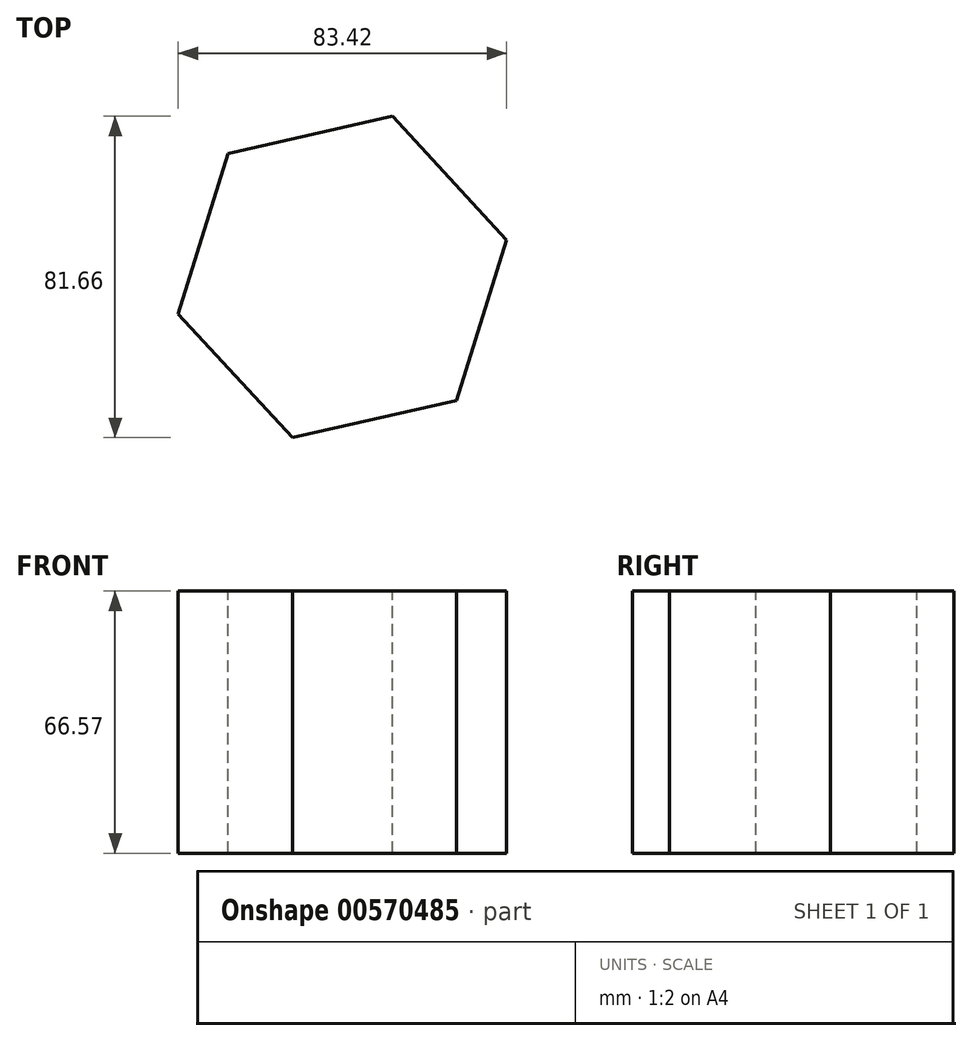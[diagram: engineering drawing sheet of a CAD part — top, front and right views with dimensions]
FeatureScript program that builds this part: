
annotation { "Feature Type Name" : "Feature", "Feature Type Description" : "" }
export const myFeature = defineFeature(function(context is Context, id is Id, definition is map)
    precondition{}
    {
        {
            var Q0;
            Q0=qCreatedBy(makeId("Top.planeOp"),FACE);
            var sketch = newSketch(context, id + "F0", { "sketchPlane" : qUnion([Q0])});
            skLineSegment(sketch, "E0.0", {"start": v(12.7, 40.83) * mm, "end": v(41.7, 9.42) * mm});
            skLineSegment(sketch, "E0.1", {"start": v(41.7, 9.42) * mm, "end": v(29.01, -31.4) * mm});
            skLineSegment(sketch, "E0.2", {"start": v(29.01, -31.4) * mm, "end": v(-12.7, -40.83) * mm});
            skLineSegment(sketch, "E0.3", {"start": v(-12.7, -40.83) * mm, "end": v(-41.7, -9.42) * mm});
            skLineSegment(sketch, "E0.4", {"start": v(-41.7, -9.42) * mm, "end": v(-29.01, 31.4) * mm});
            skLineSegment(sketch, "E0.5", {"start": v(-29.01, 31.4) * mm, "end": v(12.7, 40.83) * mm});
            skPoint(sketch, "E0.0.midPoint", {"position": v(27.2, 25.13) * mm});
            skSolve(sketch);
        }
        {
            var Q0;
            Q0=qCreatedBy(makeId("Front.planeOp"),FACE);
            var sketch = newSketch(context, id + "F1", { "sketchPlane" : qUnion([Q0])});
            skLineSegment(sketch, "E1", {"start": v(0, 0) * mm, "end": v(0, 66.57) * mm});
            skSolve(sketch);
        }
        {
            var Q0;
            Q0 = qSketchRegion(id + "F0", true);
            var Q1;
            Q1 = qConstructionFilter(qBodyType(qCreatedBy(id + "F1" ,EDGE), BodyType.WIRE), ConstructionObject.NO);
            sweep(context, id + "F2", {"profiles" : qUnion([Q0]), "path" : qUnion([Q1])});
        }
    });
